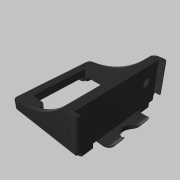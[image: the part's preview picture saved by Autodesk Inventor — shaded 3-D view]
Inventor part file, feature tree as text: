
AUTODESK INVENTOR PART (.ipt)
format: ipt  version: 2020.3 (Build 243373010, 373A)  size: 969,216 bytes
history: native  units: mm
features: other x26, extrude x8, sketch x8, fillet x5, mirror x2, projected_geometry x1
ambient origin geometry x8: Origin, YZ Plane, XZ Plane, XY Plane, X Axis, Y Axis, Z Axis, Center Point
bodies: Solid21 (feature_tree), Solid1 (feature_tree), Solid2 (feature_tree), Solid3 (feature_tree), Solid4 (feature_tree), Solid5 (feature_tree), Solid6 (feature_tree), Solid7 (feature_tree), Solid8 (feature_tree), Solid9 (feature_tree), Solid10 (feature_tree), Solid11 (feature_tree), Solid12 (feature_tree), Solid13 (feature_tree), Solid14 (feature_tree), Solid15 (feature_tree), Solid16 (feature_tree), Solid17 (feature_tree), Solid18 (feature_tree), Solid19 (feature_tree), Solid20 (feature_tree)
feature tree (50):
  other  "OT-2 Reference Model Detailed.ipt"
  other  "FOV X"
  other  "Work Point1"
  other  "FOV Center"
  extrude  "Extrusion1"  Depth=10.0mm
  extrude  "Extrusion2"  Depth=28.3mm
  fillet  "Fillet1"  Radius=1.5mm
  extrude  "Extrusion3"  Depth=1.5mm
  fillet  "Fillet2"  Radius=1.5mm
  mirror  "Mirror1"
  extrude  "Extrusion4"  Depth=25.0mm
  fillet  "Fillet3"  Radius=25.0mm
  extrude  "Extrusion8"  Depth=4.5mm
  fillet  "Fillet4"  Radius=3.5mm
  extrude  "Extrusion5"  Depth=13.0mm
  extrude  "Extrusion6"  Depth=3.5mm TaperAngle=0.0deg
  mirror  "Mirror2"
  extrude  "Extrusion7"  Depth=10.0mm
  fillet  "Fillet5"  Radius=2.0mm
  other  "Solid17::OT-2 Reference Model Detailed.ipt"
  other  "TaggingFeature1"
  other  "Solid1::OT-2 Reference Model Detailed.ipt"
  other  "Solid2::OT-2 Reference Model Detailed.ipt"
  other  "Solid3::OT-2 Reference Model Detailed.ipt"
  other  "Solid4::OT-2 Reference Model Detailed.ipt"
  other  "Solid5::OT-2 Reference Model Detailed.ipt"
  other  "Solid6::OT-2 Reference Model Detailed.ipt"
  other  "Solid7::OT-2 Reference Model Detailed.ipt"
  other  "Solid8::OT-2 Reference Model Detailed.ipt"
  other  "Solid9::OT-2 Reference Model Detailed.ipt"
  other  "Solid10::OT-2 Reference Model Detailed.ipt"
  other  "Solid11::OT-2 Reference Model Detailed.ipt"
  other  "Solid12::OT-2 Reference Model Detailed.ipt"
  other  "Solid13::OT-2 Reference Model Detailed.ipt"
  other  "Solid14::OT-2 Reference Model Detailed.ipt"
  other  "Solid16::OT-2 Reference Model Detailed.ipt"
  other  "Solid18::OT-2 Reference Model Detailed.ipt"
  other  "Solid21::OT-2 Reference Model Detailed.ipt"
  other  "Solid24::OT-2 Reference Model Detailed.ipt"
  other  "Solid26::OT-2 Reference Model Detailed.ipt"
  other  "FOV Y"
  sketch  "Sketch1"  dims[d0=10.0mm d1=16.0mm]
  sketch  "Sketch2"  dims[d2=28.3mm d3=28.3mm d4=1.5mm]
  projected_geometry  "Projected Loop1"
  sketch  "Sketch3"  dims[d5=1.5mm d6=1.5mm d7=1.5mm]
  sketch  "Sketch4"  dims[d8=1.85mm d9=25.0mm d10=25.0mm]
  sketch  "Sketch5"  dims[d11=11.0mm d12=4.5mm d13=3.5mm d14=0.0mm]
  sketch  "Sketch6"  dims[d15=3.25mm d16=13.0mm]
  sketch  "Sketch7"  dims[d17=6.5mm d18=3.5mm d19=0.0mm]
  sketch  "Sketch8"  dims[d20=2.0mm d21=6.0mm d22=2.0mm d23=0.0mm d24=2.0mm d25=2.0mm d26=1.0mm d27=20.0mm d28=0.0mm d29=2.0mm d30=2.0mm d31=6.0mm d32=6.0mm d33=6.0mm d34=6.0mm d35=2.0mm d36=0.0mm d37=40.0mm d38=2.0mm d39=0.0mm d40=6.5mm d41=0.75mm d42=0.0mm d43=2.0mm d44=10.0mm d45=0.0mm]
